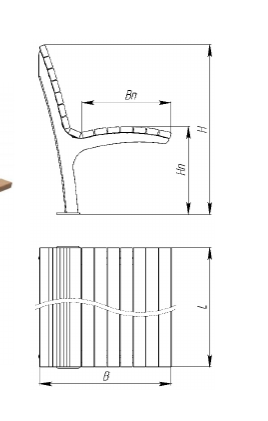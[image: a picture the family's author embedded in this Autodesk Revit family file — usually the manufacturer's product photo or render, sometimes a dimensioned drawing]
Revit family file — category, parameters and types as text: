
# Revit family: Скамейка стальная «Платиум» Арт 13260
name_source: partatom
category: Антураж
revit_build: Autodesk Revit 2018 (Build: 20180423_1000(x64)
units: mm (PartAtom-declared; Revit-internal decimal feet)

## family parameters
Всегда вертикально = Да
Источник визуального образа = Геометрия семейства
На основе рабочей плоскости = Нет
Общий = Нет
При загрузке вырезать с полостями = Нет
Точка расчета площади = Нет

## types (4) — shared parameters
URL = https://hobbyka.ru
Артикул товара = Арт. 13260
Высота = 864 мм
Группа модели = Скамейки
Изготовитель = ООО «Хоббика»
Изображение типоразмера = Скамейка стальная «Платиум» Арт 13260.jpg
Материал изделия = Сталь, дерево
Ширина = 676 мм

## per-type parameters (varying)
| type | Версия 1,5 м | Версия 1,8 м | Версия 2,0 м (2 опоры) | Версия 2,5 м (3 опоры) | Длина | Описание | Средняя опора |
| Версия 1,5 м | Да | Нет | Нет | Нет | 1500 мм | Скамейка стальная «Платиум». Версия 1,5 м | Нет |
| Версия 1,8 м | Нет | Да | Нет | Нет | 1800 мм | Скамейка стальная «Платиум». Версия 1,8 м | Нет |
| Версия 2,0 м (2 опоры) | Нет | Нет | Да | Нет | 2000 мм | Скамейка стальная «Платиум». Версия 2,0 м | Нет |
| Версия 2,5 м (3 опоры) | Нет | Нет | Нет | Да | 2500 мм | Скамейка стальная «Платиум». Версия 2,5 м с тремя опорами | Да |
